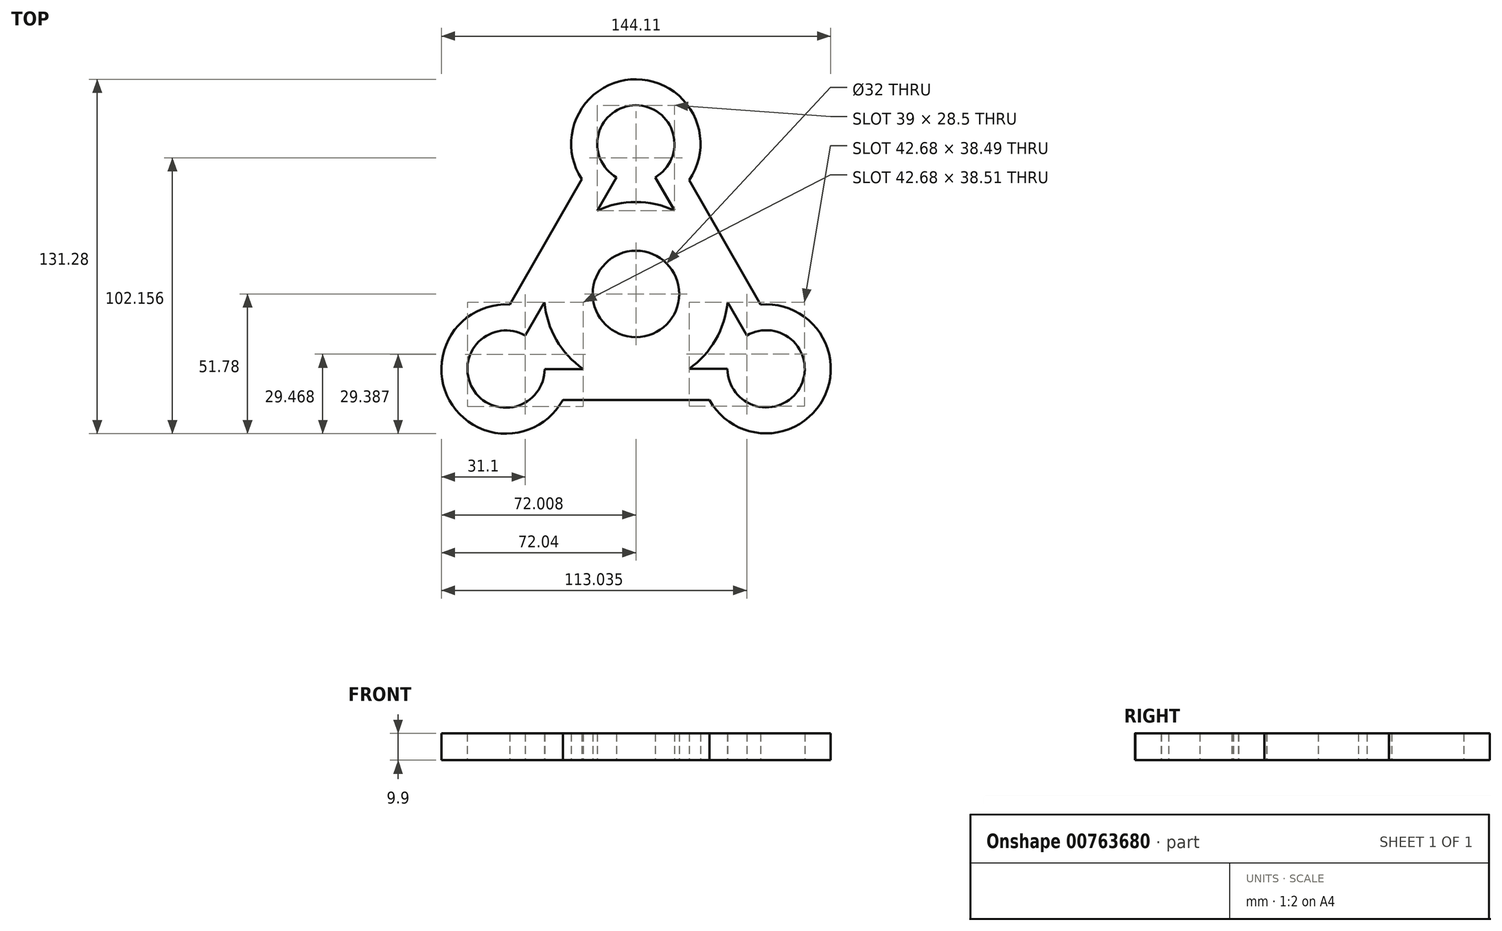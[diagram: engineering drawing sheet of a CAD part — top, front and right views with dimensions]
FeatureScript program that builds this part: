
annotation { "Feature Type Name" : "Feature", "Feature Type Description" : "" }
export const myFeature = defineFeature(function(context is Context, id is Id, definition is map)
    precondition{}
    {
        {
            var Q0;
            Q0=qCreatedBy(makeId("Top.planeOp"),FACE);
            var sketch = newSketch(context, id + "F0", { "sketchPlane" : qUnion([Q0])});
            skCircle(sketch, "E0.cCircle", {"center": v(0, 0) * mm, "radius": 27.79 * mm, "construction": true});
            skLineSegment(sketch, "E0.0", {"start": v(-0.06, 55.58) * mm, "end": v(48.16, -27.74) * mm});
            skLineSegment(sketch, "E0.1", {"start": v(48.16, -27.74) * mm, "end": v(-48.1, -27.84) * mm});
            skLineSegment(sketch, "E0.2", {"start": v(-48.1, -27.84) * mm, "end": v(-0.06, 55.58) * mm});
            skPoint(sketch, "E0.0.midPoint", {"position": v(24.05, 13.92) * mm});
            skCircle(sketch, "E1", {"center": v(-48.1, -27.84) * mm, "radius": 23.94 * mm});
            skCircle(sketch, "E2", {"center": v(48.16, -27.74) * mm, "radius": 23.9 * mm});
            skCircle(sketch, "E3", {"center": v(-0.06, 55.58) * mm, "radius": 23.93 * mm});
            skLineSegment(sketch, "E4", {"start": v(-46.74, -3.94) * mm, "end": v(-20.08, 42.47) * mm});
            skLineSegment(sketch, "E5", {"start": v(19.74, 42.15) * mm, "end": v(46.08, -3.92) * mm});
            skLineSegment(sketch, "E6", {"start": v(-27.09, -39.31) * mm, "end": v(27.24, -39.31) * mm});
            skSolve(sketch);
        }
        {
            var Q0;
            Q0 = qSketchRegion(id + "F0", true);
            extrude(context, id + "F1", {"entities" : qUnion([Q0]), "depth" : 9.9 * mm, "offsetDistance" : 25.4 * mm});
        }
        {
            var Q0;
            Q0=qCreatedBy(makeId("Top.planeOp"),FACE);
            var sketch = newSketch(context, id + "F2", { "sketchPlane" : qUnion([Q0])});
            skCircle(sketch, "E7", {"center": v(0, 0) * mm, "radius": 34.02 * mm});
            skSolve(sketch);
        }
        {
            var Q0;
            Q0 = qSketchRegion(id + "F2", true);
            extrude(context, id + "F3", {"entities" : qUnion([Q0]), "operationType" : NewBodyOperationType.ADD, "depth" : 9.9 * mm, "offsetDistance" : 25.4 * mm});
        }
        {
            var Q0;
            Q0=sQuery(id+"F0.wireOp",VERTEX,"E3.center");
            var Q1;
            Q1=sQuery(id+"F0.wireOp",VERTEX,"E0.1.start");
            var Q2;
            Q2=sQuery(id+"F0.wireOp",VERTEX,"E0.2.start");
            var Q3;
            Q3=makeQuery(id+"F1.opExtrude","SWEPT_BODY",BODY,{"disambiguationData":[OSD([sQuery(id+"F0.wireOp",EDGE,"E0.0"),sQuery(id+"F0.wireOp",EDGE,"E0.1"),sQuery(id+"F0.wireOp",EDGE,"E0.2"),sQuery(id+"F0.wireOp",EDGE,"E1"),sQuery(id+"F0.wireOp",EDGE,"E2"),sQuery(id+"F0.wireOp",EDGE,"E3"),sQuery(id+"F0.wireOp",EDGE,"E4"),sQuery(id+"F0.wireOp",EDGE,"E5"),sQuery(id+"F0.wireOp",EDGE,"E6")])]});
            hole(context, id + "F4", {"style" : HoleStyle.SIMPLE, "endStyle" : HoleEndStyle.THROUGH, "oppositeDirection" : true, "holeDiameter" : 28.6 * mm, "majorDiameter" : 6.35 * mm, "isTappedThrough" : true, "tappedDepth" : 12.7 * mm, "tapClearance" : 3, "locations" : qUnion([Q0, Q1, Q2]), "scope" : qUnion([Q3])});
        }
        {
            var Q0;
            Q0=sQuery(id+"F0.wireOp",VERTEX,"E0.cCircle.center");
            var Q1;
            Q1=makeQuery(id+"F1.opExtrude","SWEPT_BODY",BODY,{"disambiguationData":[OSD([sQuery(id+"F0.wireOp",EDGE,"E0.0"),sQuery(id+"F0.wireOp",EDGE,"E0.1"),sQuery(id+"F0.wireOp",EDGE,"E0.2"),sQuery(id+"F0.wireOp",EDGE,"E1"),sQuery(id+"F0.wireOp",EDGE,"E2"),sQuery(id+"F0.wireOp",EDGE,"E3"),sQuery(id+"F0.wireOp",EDGE,"E4"),sQuery(id+"F0.wireOp",EDGE,"E5"),sQuery(id+"F0.wireOp",EDGE,"E6")])]});
            hole(context, id + "F5", {"style" : HoleStyle.SIMPLE, "endStyle" : HoleEndStyle.THROUGH, "oppositeDirection" : true, "holeDiameter" : 32 * mm, "majorDiameter" : 6.35 * mm, "isTappedThrough" : true, "tappedDepth" : 12.7 * mm, "tapClearance" : 3, "locations" : qUnion([Q0]), "scope" : qUnion([Q1])});
        }
    });
